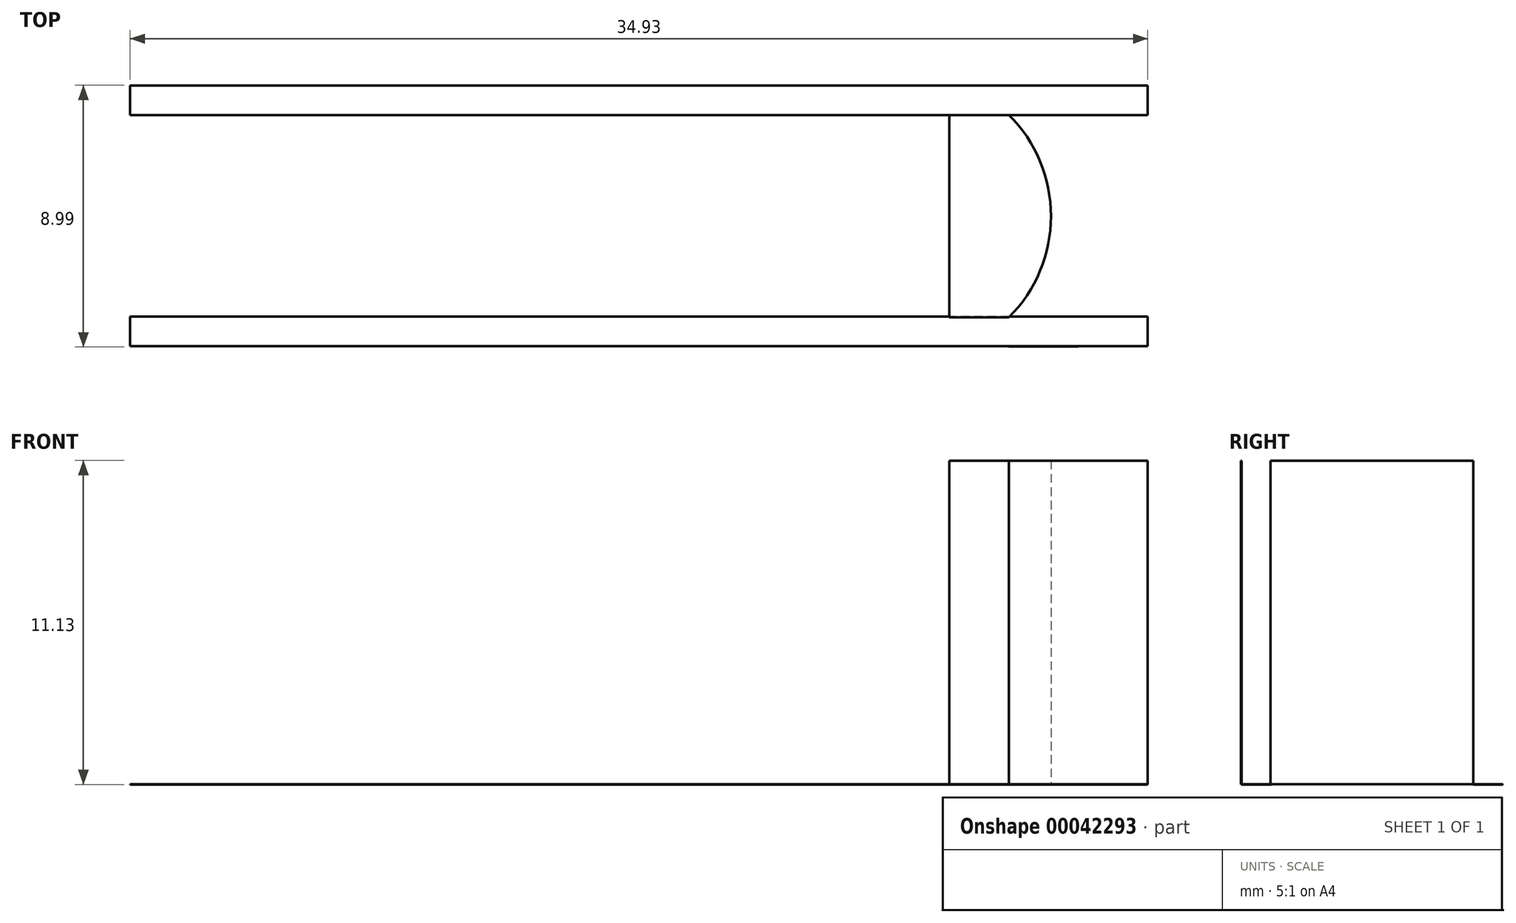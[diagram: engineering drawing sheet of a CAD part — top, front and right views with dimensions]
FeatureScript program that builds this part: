
annotation { "Feature Type Name" : "Feature", "Feature Type Description" : "" }
export const myFeature = defineFeature(function(context is Context, id is Id, definition is map)
    precondition{}
    {
        {
            var Q0;
            Q0=qCreatedBy(makeId("Top.planeOp"),FACE);
            var sketch = newSketch(context, id + "F0", { "sketchPlane" : qUnion([Q0])});
            skLineSegment(sketch, "E0", {"start": v(-24.5, 8.99) * mm, "end": v(-24.5, 0.02) * mm});
            skLineSegment(sketch, "E1", {"start": v(-24.5, 0.02) * mm, "end": v(10.43, 0.02) * mm});
            skLineSegment(sketch, "E2", {"start": v(10.43, 0.02) * mm, "end": v(10.43, 8.99) * mm});
            skLineSegment(sketch, "E3", {"start": v(10.43, 8.99) * mm, "end": v(-24.5, 8.99) * mm});
            skSolve(sketch);
        }
        {
            var Q0;
            Q0 = qSketchRegion(id + "F0", true);
            extrude(context, id + "F1", {"entities" : qUnion([Q0]), "depth" : 6 / 431.8 * mm});
        }
        {
            var Q0;
            Q0=makeQuery(id+"F1.opExtrude","SWEPT_FACE",FACE,{"disambiguationData":[OSD([sQuery(id+"F0.wireOp",EDGE,"E2")])]});
            var sketch = newSketch(context, id + "F2", { "sketchPlane" : qUnion([Q0])});
            skLineSegment(sketch, "E4", {"start": v(1.04, 0) * mm, "end": v(1.04, 7.95) * mm});
            skLineSegment(sketch, "E5", {"start": v(1.04, 7.95) * mm, "end": v(7.97, 7.95) * mm});
            skLineSegment(sketch, "E6", {"start": v(7.97, 7.95) * mm, "end": v(7.97, 0) * mm});
            skLineSegment(sketch, "E7", {"start": v(7.97, 0) * mm, "end": v(1.04, 0) * mm});
            skSolve(sketch);
        }
        {
            var Q0;
            Q0 = qSketchRegion(id + "F2", true);
            extrude(context, id + "F3", {"entities" : qUnion([Q0]), "operationType" : NewBodyOperationType.REMOVE, "endBound" : BoundingType.THROUGH_ALL, "oppositeDirection" : true, "depth" : 25.4 * mm});
        }
        {
            var Q0;
            Q0=makeQuery(id+"F1.opExtrude","CAP_FACE",FACE,{"disambiguationData":[OSD([sQuery(id+"F0.wireOp",EDGE,"E0"),sQuery(id+"F0.wireOp",EDGE,"E1"),sQuery(id+"F0.wireOp",EDGE,"E2"),sQuery(id+"F0.wireOp",EDGE,"E3")])],"isStart":false});
            var sketch = newSketch(context, id + "F4", { "sketchPlane" : qUnion([Q0])});
            skLineSegment(sketch, "E8", {"start": v(5.66, 8.99) * mm, "end": v(5.66, 0) * mm});
            skLineSegment(sketch, "E9", {"start": v(5.66, 0) * mm, "end": v(10.43, 0.02) * mm});
            skLineSegment(sketch, "E10", {"start": v(10.43, 0.02) * mm, "end": v(10.43, 8.99) * mm});
            skLineSegment(sketch, "E11", {"start": v(10.43, 8.99) * mm, "end": v(5.66, 8.99) * mm});
            skLineSegment(sketch, "E12", {"start": v(5.66, 8.99) * mm, "end": v(5.66, 7.97) * mm});
            skLineSegment(sketch, "E13", {"start": v(5.66, 0) * mm, "end": v(5.66, 1.02) * mm});
            skArc(sketch, "E14", {"start": v(5.66, 1.02) * mm, "mid": v(7.1, 4.5) * mm, "end": v(5.66, 7.97) * mm});
            skLineSegment(sketch, "E15", {"start": v(5.66, 7.97) * mm, "end": v(3.62, 7.97) * mm});
            skLineSegment(sketch, "E16", {"start": v(3.62, 7.97) * mm, "end": v(3.62, 1.02) * mm});
            skLineSegment(sketch, "E17", {"start": v(3.62, 1.02) * mm, "end": v(5.66, 1.02) * mm});
            skSolve(sketch);
        }
        {
            var Q0;
            Q0=makeQuery(id+"F4.imprint","IMPRINT",FACE,{"disambiguationData":[TD([[makeQuery(id+"F4.imprint","IMPRINT",EDGE,{"derivedFrom":sQuery(id+"F4.wireOp",EDGE,"E8")}),1.0]])]});
            var Q1;
            Q1=makeQuery(id+"F4.imprint","IMPRINT",FACE,{"disambiguationData":[TD([[makeQuery(id+"F4.imprint","IMPRINT",EDGE,{"derivedFrom":sQuery(id+"F4.wireOp",EDGE,"E8")}),-1.0]])]});
            extrude(context, id + "F5", {"entities" : qUnion([Q0, Q1]), "operationType" : NewBodyOperationType.ADD, "depth" : 11.1 * mm});
        }
    });
